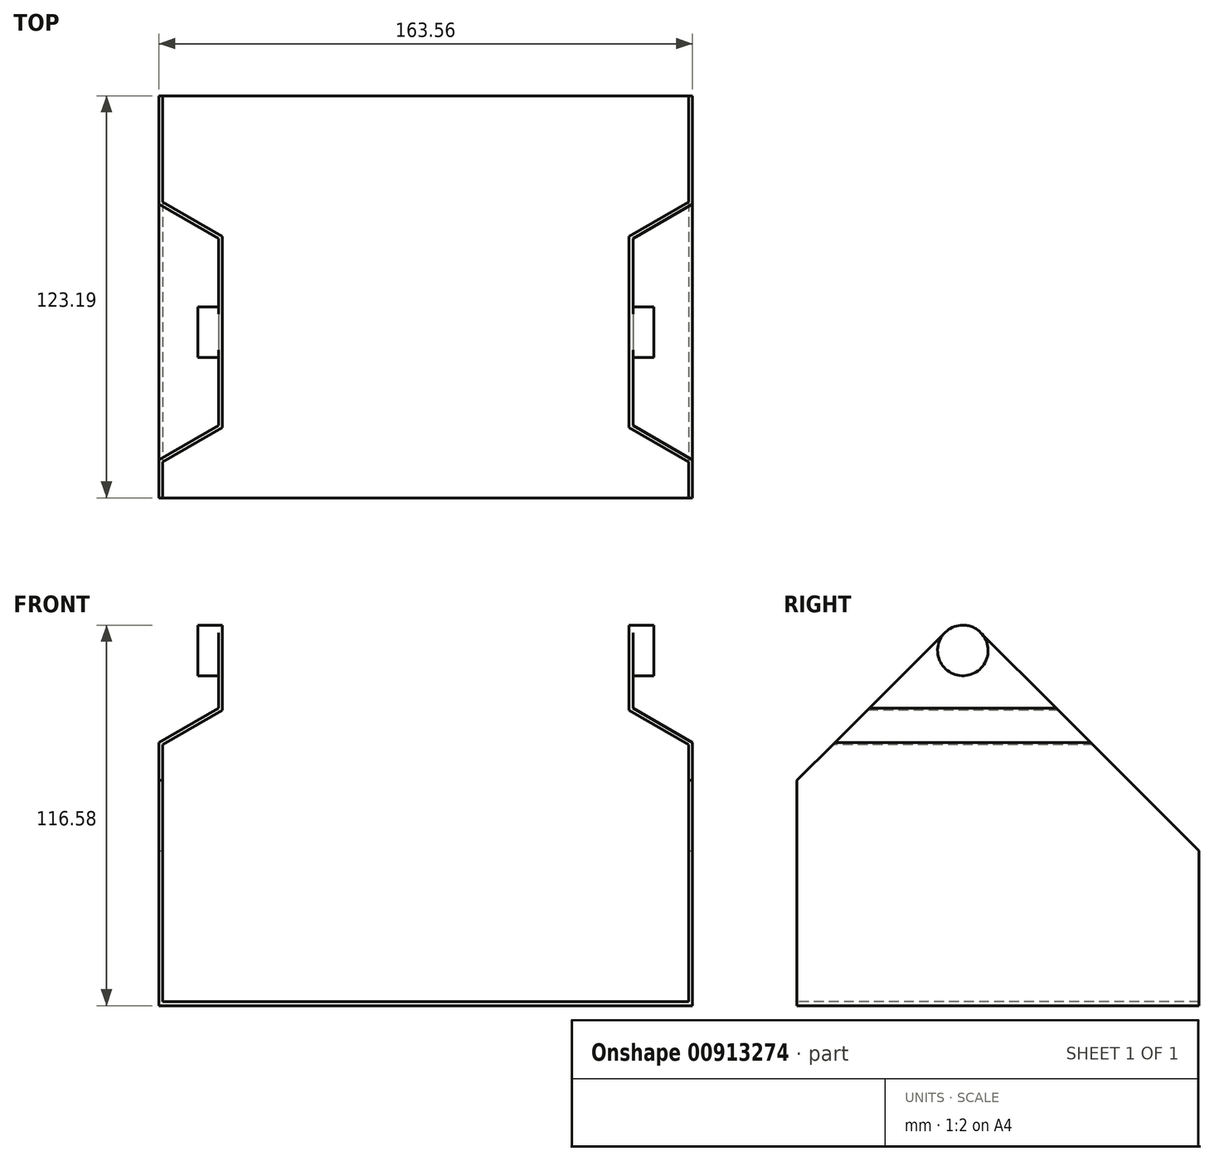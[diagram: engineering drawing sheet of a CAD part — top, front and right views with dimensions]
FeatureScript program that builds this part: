
annotation { "Feature Type Name" : "Feature", "Feature Type Description" : "" }
export const myFeature = defineFeature(function(context is Context, id is Id, definition is map)
    precondition{}
    {
        {
            var Q0;
            Q0=qCreatedBy(makeId("Front.planeOp"),FACE);
            var sketch = newSketch(context, id + "F0", { "sketchPlane" : qUnion([Q0])});
            skLineSegment(sketch, "E0.bottom", {"start": v(79.37, 36.2) * mm, "end": v(-79.38, 36.2) * mm, "construction": true});
            skLineSegment(sketch, "E0.top", {"start": v(79.38, -36.2) * mm, "end": v(-79.37, -36.2) * mm, "construction": true});
            skLineSegment(sketch, "E0.left", {"start": v(79.37, 36.2) * mm, "end": v(79.38, -36.2) * mm, "construction": true});
            skLineSegment(sketch, "E0.right", {"start": v(-79.38, 36.2) * mm, "end": v(-79.37, -36.2) * mm, "construction": true});
            skPoint(sketch, "E0.middle", {"position": v(0, 0) * mm});
            skLineSegment(sketch, "E1", {"start": v(-56.64, 36.2) * mm, "end": v(56.64, 36.2) * mm, "construction": true});
            skPoint(sketch, "E2", {"position": v(0, 36.2) * mm});
            skLineSegment(sketch, "E3", {"start": v(0, -36.2) * mm, "end": v(80.58, -36.2) * mm});
            skLineSegment(sketch, "E4", {"start": v(80.58, -36.2) * mm, "end": v(80.57, 42.55) * mm});
            skLineSegment(sketch, "E5", {"start": v(80.57, 42.55) * mm, "end": v(62.3, 53.1) * mm});
            skLineSegment(sketch, "E6", {"start": v(62.3, 53.1) * mm, "end": v(62.3, 79.19) * mm});
            skLineSegment(sketch, "E7", {"start": v(62.3, 79.19) * mm, "end": v(63.5, 79.19) * mm});
            skLineSegment(sketch, "E8", {"start": v(63.5, 79.19) * mm, "end": v(63.5, 53.79) * mm});
            skLineSegment(sketch, "E9", {"start": v(63.5, 53.79) * mm, "end": v(81.77, 43.24) * mm});
            skLineSegment(sketch, "E10", {"start": v(81.77, 43.24) * mm, "end": v(81.78, -37.4) * mm});
            skLineSegment(sketch, "E11", {"start": v(81.78, -37.4) * mm, "end": v(0, -37.4) * mm});
            skLineSegment(sketch, "E12.MirrorCS", {"start": v(-81.78, -37.4) * mm, "end": v(0, -37.4) * mm});
            skLineSegment(sketch, "E13.MirrorCS", {"start": v(-81.77, 43.24) * mm, "end": v(-81.78, -37.4) * mm});
            skLineSegment(sketch, "E14.MirrorCS", {"start": v(-80.58, -36.2) * mm, "end": v(-80.57, 42.55) * mm});
            skLineSegment(sketch, "E15.MirrorCS", {"start": v(0, -36.2) * mm, "end": v(-80.58, -36.2) * mm});
            skLineSegment(sketch, "E16.MirrorCS", {"start": v(-63.5, 53.79) * mm, "end": v(-81.77, 43.24) * mm});
            skLineSegment(sketch, "E17.MirrorCS", {"start": v(-80.57, 42.55) * mm, "end": v(-62.3, 53.1) * mm});
            skLineSegment(sketch, "E18.MirrorCS", {"start": v(-62.3, 53.1) * mm, "end": v(-62.3, 79.19) * mm});
            skLineSegment(sketch, "E19.MirrorCS", {"start": v(-63.5, 79.19) * mm, "end": v(-63.5, 53.79) * mm});
            skLineSegment(sketch, "E20.MirrorCS", {"start": v(-62.3, 79.19) * mm, "end": v(-63.5, 79.19) * mm});
            skSolve(sketch);
        }
        {
            var Q0;
            Q0=makeQuery(id+"F0.imprint","IMPRINT",FACE,{"disambiguationData":[TD([[makeQuery(id+"F0.imprint","IMPRINT",EDGE,{"derivedFrom":sQuery(id+"F0.wireOp",EDGE,"E3")}),-1.0]])]});
            extrude(context, id + "F1", {"entities" : qUnion([Q0]), "oppositeDirection" : true, "depth" : 72.39 * mm, "offsetDistance" : 25.4 * mm, "hasSecondDirection" : true, "secondDirectionOppositeDirection" : false, "secondDirectionDepth" : 50.8 * mm});
        }
        {
            var Q0;
            Q0=qCreatedBy(makeId("Right.planeOp"),FACE);
            var sketch = newSketch(context, id + "F2", { "sketchPlane" : qUnion([Q0])});
            skCircle(sketch, "E21", {"center": v(0, 71.44) * mm, "radius": 7.75 * mm});
            skSolve(sketch);
        }
        {
            var Q0;
            Q0=makeQuery(id+"F2.imprint","IMPRINT",FACE,{"disambiguationData":[TD([[makeQuery(id+"F2.imprint","IMPRINT",EDGE,{"derivedFrom":sQuery(id+"F2.wireOp",EDGE,"E21")}),1.0]])]});
            var Q1;
            Q1=makeQuery(id+"F1.opExtrude","SWEPT_FACE",FACE,{"disambiguationData":[OSD([sQuery(id+"F0.wireOp",EDGE,"E19.MirrorCS")])]});
            var Q2;
            Q2=makeQuery(id+"F1.opExtrude","SWEPT_FACE",FACE,{"disambiguationData":[OSD([sQuery(id+"F0.wireOp",EDGE,"E8")])]});
            extrude(context, id + "F3", {"entities" : qUnion([Q0]), "operationType" : NewBodyOperationType.ADD, "endBound" : BoundingType.UP_TO_SURFACE, "oppositeDirection" : true, "depth" : 25.4 * mm, "endBoundEntityFace" : qUnion([Q1]), "hasOffset" : true, "offsetDistance" : 6.35 * mm, "offsetOppositeDirection" : true, "hasSecondDirection" : true, "secondDirectionBound" : SecondDirectionBoundingType.UP_TO_SURFACE, "secondDirectionOppositeDirection" : false, "secondDirectionDepth" : 25.4 * mm, "secondDirectionBoundEntityFace" : qUnion([Q2]), "hasSecondDirectionOffset" : true, "secondDirectionOffsetDistance" : 6.35 * mm, "secondDirectionOffsetOppositeDirection" : true});
        }
        {
            var Q0;
            Q0=qCreatedBy(makeId("Front.planeOp"),FACE);
            var sketch = newSketch(context, id + "F4", { "sketchPlane" : qUnion([Q0])});
            skLineSegment(sketch, "E22.bottom", {"start": v(-62.3, 79.19) * mm, "end": v(62.3, 79.19) * mm});
            skLineSegment(sketch, "E22.top", {"start": v(-62.3, 53.1) * mm, "end": v(62.3, 53.1) * mm});
            skLineSegment(sketch, "E22.left", {"start": v(-62.3, 79.19) * mm, "end": v(-62.3, 53.1) * mm});
            skLineSegment(sketch, "E22.right", {"start": v(62.3, 79.19) * mm, "end": v(62.3, 53.1) * mm});
            skSolve(sketch);
        }
        {
            var Q0;
            Q0=makeQuery(id+"F4.imprint","IMPRINT",FACE,{"disambiguationData":[TD([[makeQuery(id+"F4.imprint","IMPRINT",EDGE,{"derivedFrom":sQuery(id+"F4.wireOp",EDGE,"E22.bottom")}),-1.0]])]});
            extrude(context, id + "F5", {"entities" : qUnion([Q0]), "operationType" : NewBodyOperationType.REMOVE, "endBound" : BoundingType.THROUGH_ALL, "oppositeDirection" : true, "depth" : 25.4 * mm, "offsetDistance" : 25.4 * mm, "hasSecondDirection" : true, "secondDirectionBound" : SecondDirectionBoundingType.THROUGH_ALL, "secondDirectionOppositeDirection" : false, "secondDirectionDepth" : 25.4 * mm});
        }
        {
            var Q0;
            Q0=qCreatedBy(makeId("Right.planeOp"),FACE);
            var sketch = newSketch(context, id + "F6", { "sketchPlane" : qUnion([Q0])});
            skLineSegment(sketch, "E23", {"start": v(-50.8, 31.6) * mm, "end": v(-5.48, 76.92) * mm});
            skLineSegment(sketch, "E24", {"start": v(-50.8, 31.6) * mm, "end": v(-50.8, 81.73) * mm});
            skLineSegment(sketch, "E25", {"start": v(-50.8, 81.73) * mm, "end": v(72.4, 81.73) * mm});
            skLineSegment(sketch, "E26", {"start": v(72.4, 81.73) * mm, "end": v(72.4, 10) * mm});
            skLineSegment(sketch, "E27", {"start": v(72.4, 10) * mm, "end": v(5.48, 76.92) * mm});
            skArc(sketch, "E28", {"start": v(-5.48, 76.92) * mm, "mid": v(0, 79.19) * mm, "end": v(5.48, 76.92) * mm});
            skSolve(sketch);
        }
        {
            var Q0;
            Q0=makeQuery(id+"F6.imprint","IMPRINT",FACE,{"disambiguationData":[TD([[makeQuery(id+"F6.imprint","IMPRINT",EDGE,{"derivedFrom":sQuery(id+"F6.wireOp",EDGE,"E23")}),1.0]])]});
            extrude(context, id + "F7", {"entities" : qUnion([Q0]), "operationType" : NewBodyOperationType.REMOVE, "endBound" : BoundingType.THROUGH_ALL, "oppositeDirection" : true, "depth" : 25.4 * mm, "offsetDistance" : 25.4 * mm, "hasSecondDirection" : true, "secondDirectionBound" : SecondDirectionBoundingType.THROUGH_ALL, "secondDirectionOppositeDirection" : false, "secondDirectionDepth" : 25.4 * mm});
        }
    });
